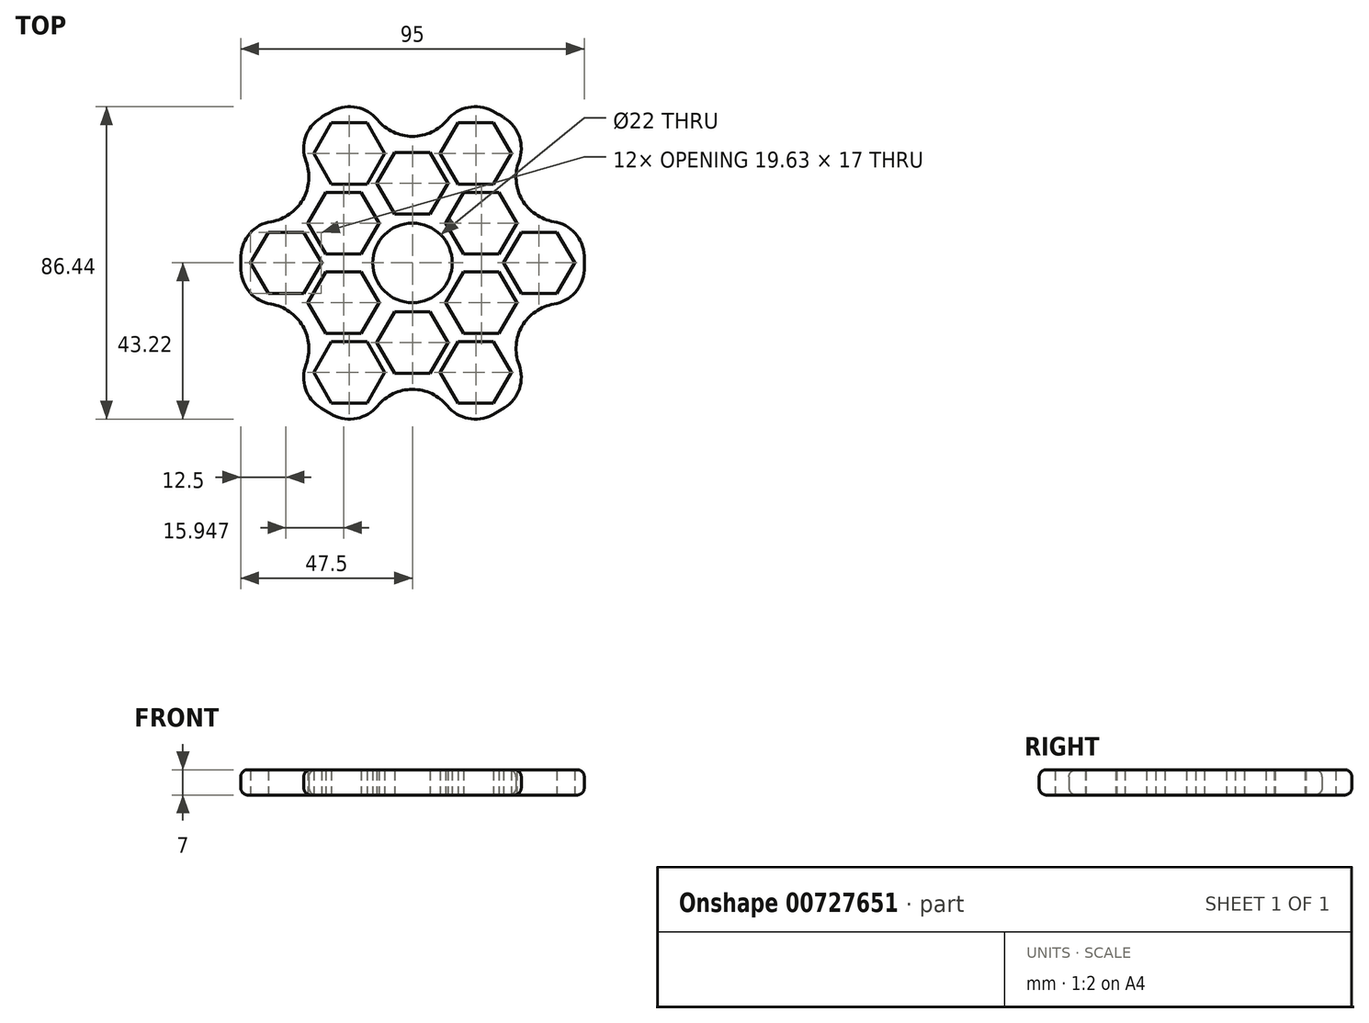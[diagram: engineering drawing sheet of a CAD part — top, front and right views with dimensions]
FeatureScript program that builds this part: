
annotation { "Feature Type Name" : "Feature", "Feature Type Description" : "" }
export const myFeature = defineFeature(function(context is Context, id is Id, definition is map)
    precondition{}
    {
        {
            var Q0;
            Q0=qCreatedBy(makeId("Top.planeOp"),FACE);
            var sketch = newSketch(context, id + "F0", { "sketchPlane" : qUnion([Q0])});
            skCircle(sketch, "E0.cCircle", {"center": v(0, 22) * mm, "radius": 8.5 * mm, "construction": true});
            skLineSegment(sketch, "E0.0", {"start": v(4.9, 13.5) * mm, "end": v(-4.9, 13.5) * mm});
            skLineSegment(sketch, "E0.1", {"start": v(-4.9, 13.5) * mm, "end": v(-9.81, 22) * mm});
            skLineSegment(sketch, "E0.2", {"start": v(-9.81, 22) * mm, "end": v(-4.9, 30.5) * mm});
            skLineSegment(sketch, "E0.3", {"start": v(-4.9, 30.5) * mm, "end": v(4.9, 30.5) * mm});
            skLineSegment(sketch, "E0.4", {"start": v(4.9, 30.5) * mm, "end": v(9.81, 22) * mm});
            skLineSegment(sketch, "E0.5", {"start": v(9.81, 22) * mm, "end": v(4.9, 13.5) * mm});
            skPoint(sketch, "E0.0.midPoint", {"position": v(0, 13.5) * mm});
            skCircle(sketch, "E1", {"center": v(0, 0) * mm, "radius": 11 * mm});
            skCircle(sketch, "E2", {"center": v(0, 0) * mm, "radius": 47.5 * mm});
            skLineSegment(sketch, "E3", {"start": v(0, 0) * mm, "end": v(-32.74, 56.72) * mm, "construction": true});
            skLineSegment(sketch, "E4", {"start": v(0, 0) * mm, "end": v(35.92, 62.2) * mm, "construction": true});
            skLineSegment(sketch, "E5.MirrorCS", {"start": v(-9.24, 11) * mm, "end": v(-14.15, 19.5) * mm});
            skLineSegment(sketch, "E6.MirrorCS", {"start": v(-14.15, 19.5) * mm, "end": v(-23.96, 19.5) * mm});
            skLineSegment(sketch, "E7.MirrorCS", {"start": v(-23.96, 19.5) * mm, "end": v(-28.87, 11) * mm});
            skLineSegment(sketch, "E8.MirrorCS", {"start": v(-28.87, 11) * mm, "end": v(-23.96, 2.5) * mm});
            skLineSegment(sketch, "E9.MirrorCS", {"start": v(-23.96, 2.5) * mm, "end": v(-14.15, 2.5) * mm});
            skLineSegment(sketch, "E10.MirrorCS", {"start": v(-14.15, 2.5) * mm, "end": v(-9.24, 11) * mm});
            skLineSegment(sketch, "E11.MirrorCS", {"start": v(9.24, 11) * mm, "end": v(14.15, 2.5) * mm});
            skLineSegment(sketch, "E12.MirrorCS", {"start": v(14.15, 2.5) * mm, "end": v(23.96, 2.5) * mm});
            skLineSegment(sketch, "E13.MirrorCS", {"start": v(23.96, 2.5) * mm, "end": v(28.87, 11) * mm});
            skLineSegment(sketch, "E14.MirrorCS", {"start": v(28.87, 11) * mm, "end": v(23.96, 19.5) * mm});
            skLineSegment(sketch, "E15.MirrorCS", {"start": v(23.96, 19.5) * mm, "end": v(14.15, 19.5) * mm});
            skLineSegment(sketch, "E16.MirrorCS", {"start": v(14.15, 19.5) * mm, "end": v(9.24, 11) * mm});
            skLineSegment(sketch, "E17.MirrorCS", {"start": v(-4.9, -30.5) * mm, "end": v(4.9, -30.5) * mm});
            skLineSegment(sketch, "E18.MirrorCS", {"start": v(4.9, -13.5) * mm, "end": v(-4.9, -13.5) * mm});
            skLineSegment(sketch, "E19.MirrorCS", {"start": v(-9.24, -11) * mm, "end": v(-14.15, -19.5) * mm});
            skLineSegment(sketch, "E20.MirrorCS", {"start": v(14.15, -19.5) * mm, "end": v(9.24, -11) * mm});
            skLineSegment(sketch, "E21.MirrorCS", {"start": v(-23.96, -2.5) * mm, "end": v(-14.15, -2.5) * mm});
            skLineSegment(sketch, "E22.MirrorCS", {"start": v(-14.15, -2.5) * mm, "end": v(-9.24, -11) * mm});
            skLineSegment(sketch, "E23.MirrorCS", {"start": v(14.15, -2.5) * mm, "end": v(23.96, -2.5) * mm});
            skLineSegment(sketch, "E24.MirrorCS", {"start": v(-14.15, -19.5) * mm, "end": v(-23.96, -19.5) * mm});
            skLineSegment(sketch, "E25.MirrorCS", {"start": v(23.96, -2.5) * mm, "end": v(28.87, -11) * mm});
            skLineSegment(sketch, "E26.MirrorCS", {"start": v(9.24, -11) * mm, "end": v(14.15, -2.5) * mm});
            skLineSegment(sketch, "E27.MirrorCS", {"start": v(23.96, -19.5) * mm, "end": v(14.15, -19.5) * mm});
            skLineSegment(sketch, "E28.MirrorCS", {"start": v(-4.9, -13.5) * mm, "end": v(-9.81, -22) * mm});
            skLineSegment(sketch, "E29.MirrorCS", {"start": v(9.81, -22) * mm, "end": v(4.9, -13.5) * mm});
            skLineSegment(sketch, "E30.MirrorCS", {"start": v(4.9, -30.5) * mm, "end": v(9.81, -22) * mm});
            skLineSegment(sketch, "E31.MirrorCS", {"start": v(28.87, -11) * mm, "end": v(23.96, -19.5) * mm});
            skPoint(sketch, "E32.MirrorP", {"position": v(0, -13.5) * mm});
            skLineSegment(sketch, "E33.MirrorCS", {"start": v(-23.96, -19.5) * mm, "end": v(-28.87, -11) * mm});
            skLineSegment(sketch, "E34.MirrorCS", {"start": v(-28.87, -11) * mm, "end": v(-23.96, -2.5) * mm});
            skLineSegment(sketch, "E35.MirrorCS", {"start": v(-9.81, -22) * mm, "end": v(-4.9, -30.5) * mm});
            skCircle(sketch, "E36.cCircle", {"center": v(-17.5, 30.31) * mm, "radius": 8.5 * mm, "construction": true});
            skLineSegment(sketch, "E36.0", {"start": v(-12.6, 21.81) * mm, "end": v(-22.4, 21.81) * mm});
            skLineSegment(sketch, "E36.1", {"start": v(-22.4, 21.81) * mm, "end": v(-27.31, 30.31) * mm});
            skLineSegment(sketch, "E36.2", {"start": v(-27.31, 30.31) * mm, "end": v(-22.4, 38.81) * mm});
            skLineSegment(sketch, "E36.3", {"start": v(-22.4, 38.81) * mm, "end": v(-12.6, 38.81) * mm});
            skLineSegment(sketch, "E36.4", {"start": v(-12.6, 38.81) * mm, "end": v(-7.69, 30.31) * mm});
            skLineSegment(sketch, "E36.5", {"start": v(-7.69, 30.31) * mm, "end": v(-12.6, 21.81) * mm});
            skPoint(sketch, "E36.0.midPoint", {"position": v(-17.5, 21.81) * mm});
            skLineSegment(sketch, "E37.MirrorCS", {"start": v(12.6, 38.81) * mm, "end": v(7.69, 30.31) * mm});
            skLineSegment(sketch, "E38.MirrorCS", {"start": v(22.4, 38.81) * mm, "end": v(12.6, 38.81) * mm});
            skLineSegment(sketch, "E39.MirrorCS", {"start": v(27.31, 30.31) * mm, "end": v(22.4, 38.81) * mm});
            skLineSegment(sketch, "E40.MirrorCS", {"start": v(22.4, 21.81) * mm, "end": v(27.31, 30.31) * mm});
            skLineSegment(sketch, "E41.MirrorCS", {"start": v(12.6, 21.81) * mm, "end": v(22.4, 21.81) * mm});
            skLineSegment(sketch, "E42.MirrorCS", {"start": v(7.69, 30.31) * mm, "end": v(12.6, 21.81) * mm});
            skLineSegment(sketch, "E43.MirrorCS", {"start": v(7.69, -30.31) * mm, "end": v(12.6, -21.81) * mm});
            skLineSegment(sketch, "E44.MirrorCS", {"start": v(12.6, -21.81) * mm, "end": v(22.4, -21.81) * mm});
            skLineSegment(sketch, "E45.MirrorCS", {"start": v(22.4, -21.81) * mm, "end": v(27.31, -30.31) * mm});
            skLineSegment(sketch, "E46.MirrorCS", {"start": v(27.31, -30.31) * mm, "end": v(22.4, -38.81) * mm});
            skLineSegment(sketch, "E47.MirrorCS", {"start": v(22.4, -38.81) * mm, "end": v(12.6, -38.81) * mm});
            skLineSegment(sketch, "E48.MirrorCS", {"start": v(12.6, -38.81) * mm, "end": v(7.69, -30.31) * mm});
            skPoint(sketch, "E49.MirrorP", {"position": v(-17.5, -21.81) * mm});
            skLineSegment(sketch, "E50.MirrorCS", {"start": v(-7.69, -30.31) * mm, "end": v(-12.6, -21.81) * mm});
            skLineSegment(sketch, "E51.MirrorCS", {"start": v(-27.31, -30.31) * mm, "end": v(-22.4, -38.81) * mm});
            skLineSegment(sketch, "E52.MirrorCS", {"start": v(-22.4, -38.81) * mm, "end": v(-12.6, -38.81) * mm});
            skLineSegment(sketch, "E53.MirrorCS", {"start": v(-22.4, -21.81) * mm, "end": v(-27.31, -30.31) * mm});
            skLineSegment(sketch, "E54.MirrorCS", {"start": v(-12.6, -21.81) * mm, "end": v(-22.4, -21.81) * mm});
            skLineSegment(sketch, "E55.MirrorCS", {"start": v(-12.6, -38.81) * mm, "end": v(-7.69, -30.31) * mm});
            skCircle(sketch, "E56.cCircle", {"center": v(-35, 0) * mm, "radius": 8.5 * mm, "construction": true});
            skLineSegment(sketch, "E56.0", {"start": v(-30.1, -8.5) * mm, "end": v(-39.9, -8.5) * mm});
            skLineSegment(sketch, "E56.1", {"start": v(-39.9, -8.5) * mm, "end": v(-44.81, 0) * mm});
            skLineSegment(sketch, "E56.2", {"start": v(-44.81, 0) * mm, "end": v(-39.9, 8.5) * mm});
            skLineSegment(sketch, "E56.3", {"start": v(-39.9, 8.5) * mm, "end": v(-30.1, 8.5) * mm});
            skLineSegment(sketch, "E56.4", {"start": v(-30.1, 8.5) * mm, "end": v(-25.19, 0) * mm});
            skLineSegment(sketch, "E56.5", {"start": v(-25.19, 0) * mm, "end": v(-30.1, -8.5) * mm});
            skPoint(sketch, "E56.0.midPoint", {"position": v(-35, -8.5) * mm});
            skLineSegment(sketch, "E57.MirrorCS", {"start": v(44.81, 0) * mm, "end": v(39.9, 8.5) * mm});
            skLineSegment(sketch, "E58.MirrorCS", {"start": v(30.1, -8.5) * mm, "end": v(39.9, -8.5) * mm});
            skLineSegment(sketch, "E59.MirrorCS", {"start": v(39.9, -8.5) * mm, "end": v(44.81, 0) * mm});
            skLineSegment(sketch, "E60.MirrorCS", {"start": v(39.9, 8.5) * mm, "end": v(30.1, 8.5) * mm});
            skPoint(sketch, "E61.MirrorP", {"position": v(35, -8.5) * mm});
            skLineSegment(sketch, "E62.MirrorCS", {"start": v(25.19, 0) * mm, "end": v(30.1, -8.5) * mm});
            skLineSegment(sketch, "E63.MirrorCS", {"start": v(30.1, 8.5) * mm, "end": v(25.19, 0) * mm});
            skLineSegment(sketch, "E64", {"start": v(0, 0) * mm, "end": v(-54.54, 31.49) * mm, "construction": true});
            skLineSegment(sketch, "E65.MirrorCS", {"start": v(0, 0) * mm, "end": v(54.54, 31.49) * mm, "construction": true});
            skLineSegment(sketch, "E66.MirrorCS", {"start": v(0, 0) * mm, "end": v(-54.54, -31.49) * mm, "construction": true});
            skLineSegment(sketch, "E67.MirrorCS", {"start": v(0, 0) * mm, "end": v(54.54, -31.49) * mm, "construction": true});
            skCircle(sketch, "E68", {"center": v(-41.14, 23.75) * mm, "radius": 12.5 * mm});
            skCircle(sketch, "E69.MirrorC", {"center": v(0, 47.5) * mm, "radius": 12.5 * mm});
            skCircle(sketch, "E70.MirrorC", {"center": v(-41.14, -23.75) * mm, "radius": 12.5 * mm});
            skCircle(sketch, "E71.MirrorC", {"center": v(0, -47.5) * mm, "radius": 12.5 * mm});
            skCircle(sketch, "E72.MirrorC", {"center": v(41.14, 23.75) * mm, "radius": 12.5 * mm});
            skCircle(sketch, "E73.MirrorC", {"center": v(41.14, -23.75) * mm, "radius": 12.5 * mm});
            skSolve(sketch);
        }
        {
            var Q0;
            Q0=makeQuery(id+"F0.imprint","IMPRINT",FACE,{"disambiguationData":[TD([[makeQuery(id+"F0.imprint","IMPRINT",EDGE,{"derivedFrom":sQuery(id+"F0.wireOp",EDGE,"E0.0")}),1.0]])]});
            extrude(context, id + "F1", {"entities" : qUnion([Q0]), "depth" : 7 * mm, "offsetDistance" : 25 * mm});
        }
        {
            var Q0;
            {var subQ0=sQuery(id+"F0.wireOp",EDGE,"E73.MirrorC");var subQ1=sQuery(id+"F0.wireOp",EDGE,"E2");Q0=makeQuery(id+"F1.opExtrude","SWEPT_EDGE",EDGE,{"disambiguationData":[OSD([subQ1,subQ0]),TDD([makeQuery(id+"F0.imprint","INTERSECT",VERTEX,{"disambiguationData":[OD(0.0)],"derivedFrom":[subQ1,subQ0]})])]});}
            var Q1;
            {var subQ0=sQuery(id+"F0.wireOp",EDGE,"E73.MirrorC");var subQ1=sQuery(id+"F0.wireOp",EDGE,"E2");Q1=makeQuery(id+"F1.opExtrude","SWEPT_EDGE",EDGE,{"disambiguationData":[OSD([subQ1,subQ0]),TDD([makeQuery(id+"F0.imprint","INTERSECT",VERTEX,{"disambiguationData":[OD(1.0)],"derivedFrom":[subQ1,subQ0]})])]});}
            var Q2;
            {var subQ0=sQuery(id+"F0.wireOp",EDGE,"E72.MirrorC");var subQ1=sQuery(id+"F0.wireOp",EDGE,"E2");Q2=makeQuery(id+"F1.opExtrude","SWEPT_EDGE",EDGE,{"disambiguationData":[OSD([subQ1,subQ0]),TDD([makeQuery(id+"F0.imprint","INTERSECT",VERTEX,{"disambiguationData":[OD(1.0)],"derivedFrom":[subQ1,subQ0]})])]});}
            var Q3;
            {var subQ0=sQuery(id+"F0.wireOp",EDGE,"E72.MirrorC");var subQ1=sQuery(id+"F0.wireOp",EDGE,"E2");Q3=makeQuery(id+"F1.opExtrude","SWEPT_EDGE",EDGE,{"disambiguationData":[OSD([subQ1,subQ0]),TDD([makeQuery(id+"F0.imprint","INTERSECT",VERTEX,{"disambiguationData":[OD(0.0)],"derivedFrom":[subQ1,subQ0]})])]});}
            var Q4;
            {var subQ0=sQuery(id+"F0.wireOp",EDGE,"E69.MirrorC");var subQ1=sQuery(id+"F0.wireOp",EDGE,"E2");Q4=makeQuery(id+"F1.opExtrude","SWEPT_EDGE",EDGE,{"disambiguationData":[OSD([subQ1,subQ0]),TDD([makeQuery(id+"F0.imprint","INTERSECT",VERTEX,{"disambiguationData":[OD(0.0)],"derivedFrom":[subQ1,subQ0]})])]});}
            var Q5;
            {var subQ0=sQuery(id+"F0.wireOp",EDGE,"E69.MirrorC");var subQ1=sQuery(id+"F0.wireOp",EDGE,"E2");Q5=makeQuery(id+"F1.opExtrude","SWEPT_EDGE",EDGE,{"disambiguationData":[OSD([subQ1,subQ0]),TDD([makeQuery(id+"F0.imprint","INTERSECT",VERTEX,{"disambiguationData":[OD(1.0)],"derivedFrom":[subQ1,subQ0]})])]});}
            var Q6;
            {var subQ0=sQuery(id+"F0.wireOp",EDGE,"E68");var subQ1=sQuery(id+"F0.wireOp",EDGE,"E2");Q6=makeQuery(id+"F1.opExtrude","SWEPT_EDGE",EDGE,{"disambiguationData":[OSD([subQ1,subQ0]),TDD([makeQuery(id+"F0.imprint","INTERSECT",VERTEX,{"disambiguationData":[OD(0.0)],"derivedFrom":[subQ1,subQ0]})])]});}
            var Q7;
            {var subQ0=sQuery(id+"F0.wireOp",EDGE,"E68");var subQ1=sQuery(id+"F0.wireOp",EDGE,"E2");Q7=makeQuery(id+"F1.opExtrude","SWEPT_EDGE",EDGE,{"disambiguationData":[OSD([subQ1,subQ0]),TDD([makeQuery(id+"F0.imprint","INTERSECT",VERTEX,{"disambiguationData":[OD(1.0)],"derivedFrom":[subQ1,subQ0]})])]});}
            var Q8;
            {var subQ0=sQuery(id+"F0.wireOp",EDGE,"E70.MirrorC");var subQ1=sQuery(id+"F0.wireOp",EDGE,"E2");Q8=makeQuery(id+"F1.opExtrude","SWEPT_EDGE",EDGE,{"disambiguationData":[OSD([subQ1,subQ0]),TDD([makeQuery(id+"F0.imprint","INTERSECT",VERTEX,{"disambiguationData":[OD(0.0)],"derivedFrom":[subQ1,subQ0]})])]});}
            var Q9;
            {var subQ0=sQuery(id+"F0.wireOp",EDGE,"E70.MirrorC");var subQ1=sQuery(id+"F0.wireOp",EDGE,"E2");Q9=makeQuery(id+"F1.opExtrude","SWEPT_EDGE",EDGE,{"disambiguationData":[OSD([subQ1,subQ0]),TDD([makeQuery(id+"F0.imprint","INTERSECT",VERTEX,{"disambiguationData":[OD(1.0)],"derivedFrom":[subQ1,subQ0]})])]});}
            var Q10;
            {var subQ0=sQuery(id+"F0.wireOp",EDGE,"E71.MirrorC");var subQ1=sQuery(id+"F0.wireOp",EDGE,"E2");Q10=makeQuery(id+"F1.opExtrude","SWEPT_EDGE",EDGE,{"disambiguationData":[OSD([subQ1,subQ0]),TDD([makeQuery(id+"F0.imprint","INTERSECT",VERTEX,{"disambiguationData":[OD(0.0)],"derivedFrom":[subQ1,subQ0]})])]});}
            var Q11;
            {var subQ0=sQuery(id+"F0.wireOp",EDGE,"E71.MirrorC");var subQ1=sQuery(id+"F0.wireOp",EDGE,"E2");Q11=makeQuery(id+"F1.opExtrude","SWEPT_EDGE",EDGE,{"disambiguationData":[OSD([subQ1,subQ0]),TDD([makeQuery(id+"F0.imprint","INTERSECT",VERTEX,{"disambiguationData":[OD(1.0)],"derivedFrom":[subQ1,subQ0]})])]});}
            fillet(context, id + "F2", {"entities" : qUnion([Q0, Q1, Q2, Q3, Q4, Q5, Q6, Q7, Q8, Q9, Q10, Q11]), "radius" : 10 * mm, "tangentPropagation" : true, "allowEdgeOverflow" : false});
        }
        {
            var Q0;
            Q0=makeQuery(id+"F1.opExtrude","CAP_EDGE",EDGE,{"disambiguationData":[OSD([sQuery(id+"F0.wireOp",EDGE,"E68")])],"isStart":false});
            var Q1;
            Q1=makeQuery(id+"F1.opExtrude","CAP_EDGE",EDGE,{"disambiguationData":[OSD([sQuery(id+"F0.wireOp",EDGE,"E68")])],"isStart":true});
            fillet(context, id + "F3", {"entities" : qUnion([Q0, Q1]), "radius" : 2 * mm, "tangentPropagation" : true, "allowEdgeOverflow" : false});
        }
    });
